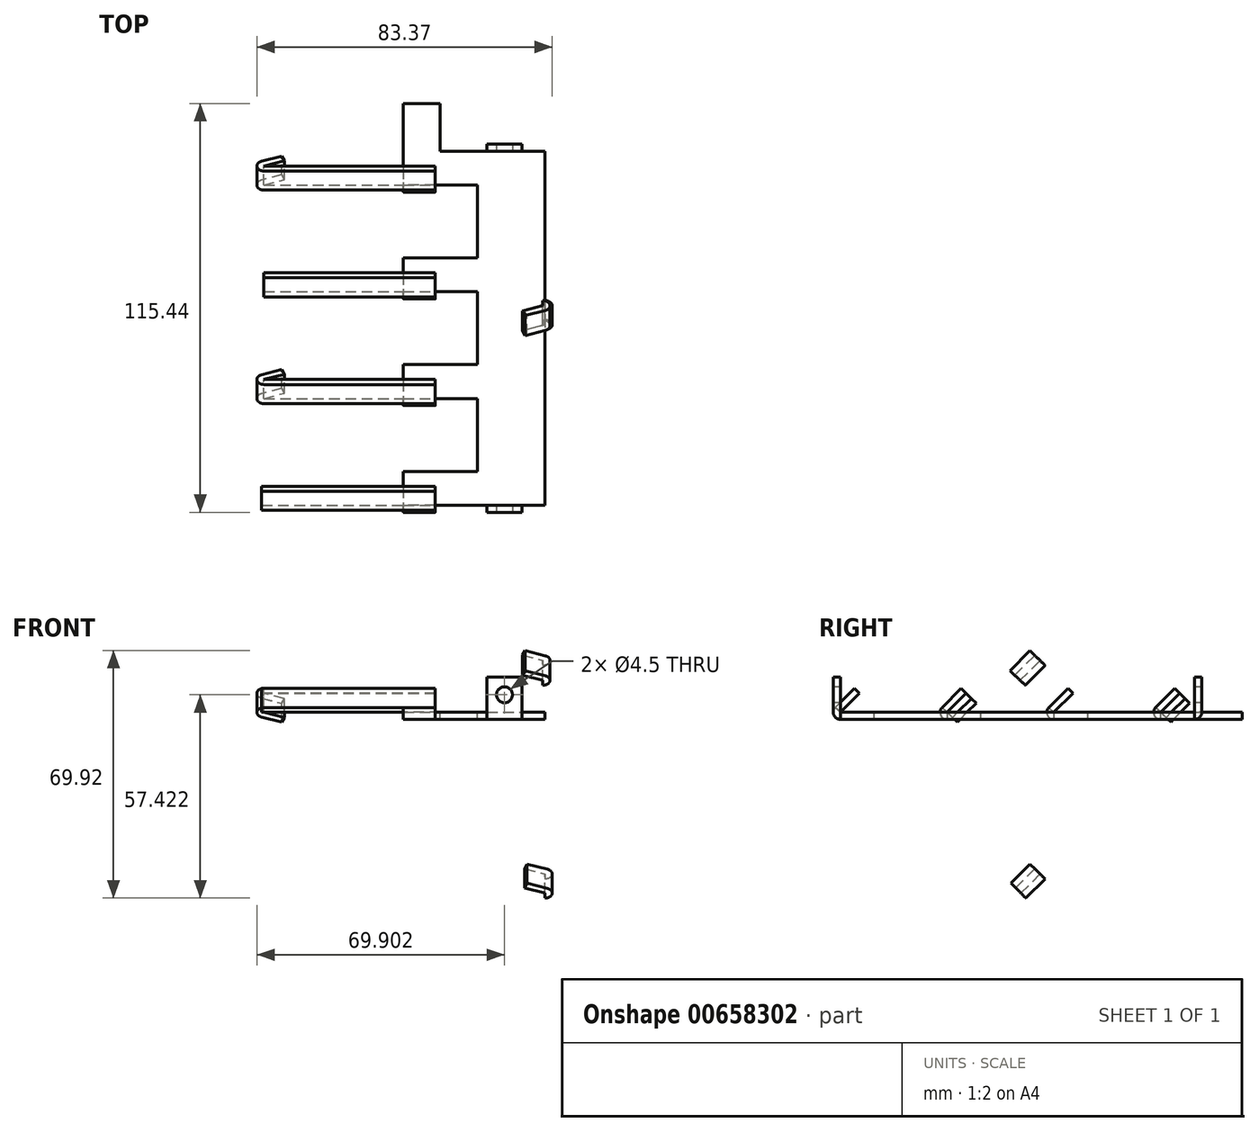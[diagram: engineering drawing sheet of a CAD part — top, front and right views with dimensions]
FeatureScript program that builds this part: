
annotation { "Feature Type Name" : "Feature", "Feature Type Description" : "" }
export const myFeature = defineFeature(function(context is Context, id is Id, definition is map)
    precondition{}
    {
        {
            var Q0;
            Q0=qCreatedBy(makeId("Top.planeOp"),FACE);
            var sketch = newSketch(context, id + "F0", { "sketchPlane" : qUnion([Q0])});
            skLineSegment(sketch, "E0", {"start": v(40, 50) * mm, "end": v(40, -50) * mm});
            skLineSegment(sketch, "E1", {"start": v(10.42, 50) * mm, "end": v(40, 50) * mm});
            skLineSegment(sketch, "E2", {"start": v(0, 50) * mm, "end": v(0, 40.43) * mm});
            skLineSegment(sketch, "E3", {"start": v(20.84, 40.43) * mm, "end": v(20.84, 19.86) * mm});
            skLineSegment(sketch, "E4", {"start": v(0, 19.86) * mm, "end": v(0, 10.29) * mm});
            skLineSegment(sketch, "E5", {"start": v(20.84, 10.29) * mm, "end": v(20.84, -10.29) * mm});
            skLineSegment(sketch, "E6", {"start": v(20.84, -10.29) * mm, "end": v(0, -10.29) * mm});
            skLineSegment(sketch, "E7", {"start": v(0, -10.29) * mm, "end": v(0, -19.86) * mm});
            skLineSegment(sketch, "E8", {"start": v(20.84, -19.86) * mm, "end": v(20.84, -40.43) * mm});
            skLineSegment(sketch, "E9", {"start": v(20.84, -40.43) * mm, "end": v(0, -40.43) * mm});
            skLineSegment(sketch, "E10", {"start": v(0, -40.43) * mm, "end": v(0, -50) * mm});
            skLineSegment(sketch, "E11", {"start": v(20.84, 19.86) * mm, "end": v(0, 19.86) * mm});
            skLineSegment(sketch, "E12", {"start": v(0, 40.43) * mm, "end": v(20.84, 40.43) * mm});
            skLineSegment(sketch, "E13", {"start": v(0, 10.29) * mm, "end": v(20.84, 10.29) * mm});
            skLineSegment(sketch, "E14", {"start": v(0, -19.86) * mm, "end": v(20.84, -19.86) * mm});
            skLineSegment(sketch, "E15", {"start": v(0, -50) * mm, "end": v(40, -50) * mm});
            skPoint(sketch, "E16.endSnap0", {"position": v(10.42, 40.43) * mm});
            skLineSegment(sketch, "E17", {"start": v(10.42, 50) * mm, "end": v(10.42, 63.44) * mm});
            skLineSegment(sketch, "E18", {"start": v(10.42, 63.44) * mm, "end": v(0, 63.44) * mm});
            skLineSegment(sketch, "E19", {"start": v(0, 63.44) * mm, "end": v(0, 50) * mm});
            skSolve(sketch);
        }
        {
            var Q0;
            Q0=makeQuery(id+"F0.imprint","IMPRINT",FACE,{"disambiguationData":[TD([[makeQuery(id+"F0.imprint","IMPRINT",EDGE,{"derivedFrom":sQuery(id+"F0.wireOp",EDGE,"E0")}),-1.0]])]});
            extrude(context, id + "F1", {"entities" : qUnion([Q0]), "endBound" : BoundingType.SYMMETRIC, "oppositeDirection" : true, "depth" : 2 * mm, "offsetDistance" : 25.4 * mm, "hasSecondDirection" : true, "secondDirectionOppositeDirection" : false, "secondDirectionDepth" : 0.76 * mm});
        }
        {
            var Q0;
            Q0=qCreatedBy(makeId("Right.planeOp"),FACE);
            var sketch = newSketch(context, id + "F2", { "sketchPlane" : qUnion([Q0])});
            skLineSegment(sketch, "E20", {"start": v(-50, 1) * mm, "end": v(-44.63, 6.37) * mm});
            skLineSegment(sketch, "E21", {"start": v(-44.63, 6.37) * mm, "end": v(-46.05, 7.78) * mm});
            skArc(sketch, "E22", {"start": v(-51.45, 2.37) * mm, "mid": v(-51.84, 0.2) * mm, "end": v(-50, -1) * mm});
            skLineSegment(sketch, "E23", {"start": v(-51.45, 2.37) * mm, "end": v(-46.05, 7.78) * mm});
            skLineSegment(sketch, "E24", {"start": v(-50, 1) * mm, "end": v(-50, -1) * mm});
            skLineSegment(sketch, "E25", {"start": v(-50, 1) * mm, "end": v(-51.45, 2.37) * mm});
            skSolve(sketch);
        }
        {
            var Q0;
            {var subQ1=sQuery(id+"F2.wireOp",EDGE,"E20");Q0=makeQuery(id+"F2.imprint","IMPRINT",FACE,{"disambiguationData":[TD([[makeQuery(id+"F2.imprint","IMPRINT",EDGE,{"derivedFrom":subQ1}),1.0]])]});}
            extrude(context, id + "F3", {"entities" : qUnion([Q0]), "operationType" : NewBodyOperationType.ADD, "oppositeDirection" : true, "depth" : 40 * mm, "offsetDistance" : 25.4 * mm});
        }
        {
            var Q0;
            Q0=makeQuery(id+"F3.opExtrude","SWEPT_FACE",FACE,{"disambiguationData":[OSD([sQuery(id+"F2.wireOp",EDGE,"E21")])]});
            var sketch = newSketch(context, id + "F4", { "sketchPlane" : qUnion([Q0])});
            skLineSegment(sketch, "E26", {"start": v(-40.68, -34.18) * mm, "end": v(-34.93, -32.09) * mm});
            skLineSegment(sketch, "E27", {"start": v(-34.93, -32.09) * mm, "end": v(-34.25, -33.97) * mm});
            skLineSegment(sketch, "E28", {"start": v(-34.25, -33.97) * mm, "end": v(-40, -36.06) * mm});
            skArc(sketch, "E29", {"start": v(-40.68, -34.18) * mm, "mid": v(-41.97, -36.4) * mm, "end": v(-40, -38.06) * mm});
            skLineSegment(sketch, "E30", {"start": v(-40, -36.06) * mm, "end": v(-40, -38.06) * mm});
            skSolve(sketch);
        }
        {
            var Q0;
            Q0=makeQuery(id+"F4.imprint","IMPRINT",FACE,{"disambiguationData":[TD([[makeQuery(id+"F4.imprint","IMPRINT",EDGE,{"derivedFrom":sQuery(id+"F4.wireOp",EDGE,"E26")}),-1.0]])]});
            extrude(context, id + "F5", {"entities" : qUnion([Q0]), "operationType" : NewBodyOperationType.ADD, "oppositeDirection" : true, "depth" : 7.65 * mm, "offsetDistance" : 25.4 * mm});
        }
        {
            var Q0;
            Q0=qCreatedBy(makeId("Right.planeOp"),FACE);
            var sketch = newSketch(context, id + "F6", { "sketchPlane" : qUnion([Q0])});
            skLineSegment(sketch, "E31", {"start": v(-19.86, 1) * mm, "end": v(-14.49, 6.36) * mm});
            skLineSegment(sketch, "E32", {"start": v(-14.49, 6.36) * mm, "end": v(-15.9, 7.78) * mm});
            skArc(sketch, "E33", {"start": v(-21.3, 2.37) * mm, "mid": v(-21.7, 0.2) * mm, "end": v(-19.86, -1) * mm});
            skLineSegment(sketch, "E34", {"start": v(-21.3, 2.37) * mm, "end": v(-15.9, 7.78) * mm});
            skLineSegment(sketch, "E35", {"start": v(-19.86, 1) * mm, "end": v(-19.86, -1) * mm});
            skLineSegment(sketch, "E36", {"start": v(-19.86, 1) * mm, "end": v(-21.3, 2.37) * mm});
            skSolve(sketch);
        }
        {
            var Q0;
            Q0=qCreatedBy(makeId("Right.planeOp"),FACE);
            var sketch = newSketch(context, id + "F7", { "sketchPlane" : qUnion([Q0])});
            skLineSegment(sketch, "E37", {"start": v(10.29, 1) * mm, "end": v(15.66, 6.36) * mm});
            skLineSegment(sketch, "E38", {"start": v(15.66, 6.36) * mm, "end": v(14.24, 7.78) * mm});
            skArc(sketch, "E39", {"start": v(8.84, 2.37) * mm, "mid": v(8.45, 0.2) * mm, "end": v(10.29, -1) * mm});
            skLineSegment(sketch, "E40", {"start": v(8.84, 2.37) * mm, "end": v(14.24, 7.78) * mm});
            skLineSegment(sketch, "E41", {"start": v(10.29, 1) * mm, "end": v(10.29, -1) * mm});
            skLineSegment(sketch, "E42", {"start": v(10.29, 1) * mm, "end": v(8.84, 2.37) * mm});
            skLineSegment(sketch, "E43", {"start": v(40.43, 1) * mm, "end": v(45.8, 6.37) * mm});
            skLineSegment(sketch, "E44", {"start": v(45.8, 6.37) * mm, "end": v(44.39, 7.78) * mm});
            skArc(sketch, "E45", {"start": v(38.98, 2.37) * mm, "mid": v(38.6, 0.2) * mm, "end": v(40.43, -1) * mm});
            skLineSegment(sketch, "E46", {"start": v(38.98, 2.37) * mm, "end": v(44.39, 7.78) * mm});
            skLineSegment(sketch, "E47", {"start": v(40.43, 1) * mm, "end": v(40.43, -1) * mm});
            skLineSegment(sketch, "E48", {"start": v(40.43, 1) * mm, "end": v(38.98, 2.37) * mm});
            skSolve(sketch);
        }
        {
            var Q0;
            Q0 = qSketchRegion(id + "F6", true);
            var Q1;
            {var subQ1=sQuery(id+"F2.wireOp",EDGE,"E20");Q1=makeQuery(id+"F2.imprint","IMPRINT",FACE,{"disambiguationData":[TD([[makeQuery(id+"F2.imprint","IMPRINT",EDGE,{"derivedFrom":subQ1}),1.0]])]});}
            var Q2;
            {var subQ0=sQuery(id+"F2.wireOp",EDGE,"E22");Q2=makeQuery(id+"F2.imprint","IMPRINT",FACE,{"disambiguationData":[TD([[makeQuery(id+"F2.imprint","IMPRINT",EDGE,{"derivedFrom":subQ0}),1.0]])]});}
            var Q3;
            {var subQ1=sQuery(id+"F7.wireOp",EDGE,"E37");Q3=makeQuery(id+"F7.imprint","IMPRINT",FACE,{"disambiguationData":[TD([[makeQuery(id+"F7.imprint","IMPRINT",EDGE,{"derivedFrom":subQ1}),1.0]])]});}
            var Q4;
            {var subQ0=sQuery(id+"F7.wireOp",EDGE,"E39");Q4=makeQuery(id+"F7.imprint","IMPRINT",FACE,{"disambiguationData":[TD([[makeQuery(id+"F7.imprint","IMPRINT",EDGE,{"derivedFrom":subQ0}),1.0]])]});}
            var Q5;
            {var subQ1=sQuery(id+"F7.wireOp",EDGE,"E43");Q5=makeQuery(id+"F7.imprint","IMPRINT",FACE,{"disambiguationData":[TD([[makeQuery(id+"F7.imprint","IMPRINT",EDGE,{"derivedFrom":subQ1}),1.0]])]});}
            var Q6;
            {var subQ0=sQuery(id+"F7.wireOp",EDGE,"E45");Q6=makeQuery(id+"F7.imprint","IMPRINT",FACE,{"disambiguationData":[TD([[makeQuery(id+"F7.imprint","IMPRINT",EDGE,{"derivedFrom":subQ0}),1.0]])]});}
            var Q7;
            Q7=makeQuery(id+"FUqeAPM6QKtiatm_4.opExtrude","CAP_FACE",FACE,{"disambiguationData":[OSD([sQuery(id+"F2.wireOp",EDGE,"E20"),sQuery(id+"F2.wireOp",EDGE,"E21"),sQuery(id+"F2.wireOp",EDGE,"E22"),sQuery(id+"F2.wireOp",EDGE,"E23"),sQuery(id+"F2.wireOp",EDGE,"E24")])],"isStart":false});
            extrude(context, id + "F8", {"entities" : qUnion([Q0, Q1, Q2, Q3, Q4, Q5, Q6]), "operationType" : NewBodyOperationType.ADD, "depth" : 9 * mm, "endBoundEntityFace" : qUnion([Q7]), "offsetDistance" : 25.4 * mm});
        }
        {
            var Q0;
            {var subQ1=sQuery(id+"F6.wireOp",EDGE,"E31");Q0=makeQuery(id+"F6.imprint","IMPRINT",FACE,{"disambiguationData":[TD([[makeQuery(id+"F6.imprint","IMPRINT",EDGE,{"derivedFrom":subQ1}),1.0]])]});}
            var Q1;
            {var subQ1=sQuery(id+"F7.wireOp",EDGE,"E37");Q1=makeQuery(id+"F7.imprint","IMPRINT",FACE,{"disambiguationData":[TD([[makeQuery(id+"F7.imprint","IMPRINT",EDGE,{"derivedFrom":subQ1}),1.0]])]});}
            var Q2;
            {var subQ1=sQuery(id+"F7.wireOp",EDGE,"E43");Q2=makeQuery(id+"F7.imprint","IMPRINT",FACE,{"disambiguationData":[TD([[makeQuery(id+"F7.imprint","IMPRINT",EDGE,{"derivedFrom":subQ1}),1.0]])]});}
            extrude(context, id + "F9", {"entities" : qUnion([Q0, Q1, Q2]), "operationType" : NewBodyOperationType.ADD, "oppositeDirection" : true, "depth" : 39.37 * mm, "offsetDistance" : 25.4 * mm});
        }
        {
            var Q0;
            {var subQ0=sQuery(id+"F6.wireOp",EDGE,"E32");Q0=makeQuery(id+"F9.boolean.opBoolean","MERGE",FACE,{"derivedFrom":[makeQuery(id+"F8.opExtrude","SWEPT_FACE",FACE,{"disambiguationData":[OSD([subQ0])]}),makeQuery(id+"F9.opExtrude","SWEPT_FACE",FACE,{"disambiguationData":[OSD([subQ0])]})]});}
            var sketch = newSketch(context, id + "F10", { "sketchPlane" : qUnion([Q0])});
            skLineSegment(sketch, "E49", {"start": v(40.05, 12.86) * mm, "end": v(34.3, 10.77) * mm});
            skLineSegment(sketch, "E50", {"start": v(34.3, 10.77) * mm, "end": v(33.62, 12.65) * mm});
            skLineSegment(sketch, "E51", {"start": v(33.62, 12.65) * mm, "end": v(39.37, 14.74) * mm});
            skArc(sketch, "E52", {"start": v(40.05, 12.86) * mm, "mid": v(41.34, 15.1) * mm, "end": v(39.37, 16.74) * mm});
            skLineSegment(sketch, "E53", {"start": v(39.37, 14.74) * mm, "end": v(39.37, 16.74) * mm});
            skSolve(sketch);
        }
        {
            var Q0;
            Q0 = qSketchRegion(id + "F10", true);
            var Q1;
            Q1=makeQuery(id+"F9.opExtrude","SWEPT_FACE",FACE,{"disambiguationData":[OSD([sQuery(id+"F6.wireOp",EDGE,"E36")])]});
            extrude(context, id + "F11", {"entities" : qUnion([Q0]), "operationType" : NewBodyOperationType.ADD, "endBound" : BoundingType.UP_TO_SURFACE, "oppositeDirection" : true, "depth" : 25.4 * mm, "endBoundEntityFace" : qUnion([Q1]), "offsetDistance" : 25.4 * mm});
        }
        {
            var Q0;
            {var subQ0=sQuery(id+"F7.wireOp",EDGE,"E38");Q0=makeQuery(id+"F9.boolean.opBoolean","MERGE",FACE,{"derivedFrom":[makeQuery(id+"F8.opExtrude","SWEPT_FACE",FACE,{"disambiguationData":[OSD([subQ0])]}),makeQuery(id+"F9.opExtrude","SWEPT_FACE",FACE,{"disambiguationData":[OSD([subQ0])]})]});}
            var sketch = newSketch(context, id + "F12", { "sketchPlane" : qUnion([Q0])});
            skLineSegment(sketch, "E54", {"start": v(-40.05, 8.45) * mm, "end": v(-34.3, 10.55) * mm});
            skLineSegment(sketch, "E55", {"start": v(-34.3, 10.55) * mm, "end": v(-33.62, 8.67) * mm});
            skLineSegment(sketch, "E56", {"start": v(-33.62, 8.67) * mm, "end": v(-39.37, 6.57) * mm});
            skArc(sketch, "E57", {"start": v(-40.05, 8.45) * mm, "mid": v(-41.34, 6.22) * mm, "end": v(-39.37, 4.57) * mm});
            skLineSegment(sketch, "E58", {"start": v(-39.37, 6.57) * mm, "end": v(-39.37, 4.57) * mm});
            skSolve(sketch);
        }
        {
            var Q0;
            Q0 = qSketchRegion(id + "F12", true);
            var Q1;
            Q1=makeQuery(id+"F9.opExtrude","SWEPT_FACE",FACE,{"disambiguationData":[OSD([sQuery(id+"F7.wireOp",EDGE,"E42")])]});
            extrude(context, id + "F13", {"entities" : qUnion([Q0]), "operationType" : NewBodyOperationType.ADD, "endBound" : BoundingType.UP_TO_SURFACE, "oppositeDirection" : true, "depth" : 25.4 * mm, "endBoundEntityFace" : qUnion([Q1]), "offsetDistance" : 25.4 * mm});
        }
        {
            var Q0;
            {var subQ0=sQuery(id+"F7.wireOp",EDGE,"E44");Q0=makeQuery(id+"F9.boolean.opBoolean","MERGE",FACE,{"derivedFrom":[makeQuery(id+"F8.opExtrude","SWEPT_FACE",FACE,{"disambiguationData":[OSD([subQ0])]}),makeQuery(id+"F9.opExtrude","SWEPT_FACE",FACE,{"disambiguationData":[OSD([subQ0])]})]});}
            var sketch = newSketch(context, id + "F14", { "sketchPlane" : qUnion([Q0])});
            skLineSegment(sketch, "E59", {"start": v(40.05, -29.76) * mm, "end": v(34.3, -31.86) * mm});
            skLineSegment(sketch, "E60", {"start": v(34.3, -31.86) * mm, "end": v(33.62, -29.98) * mm});
            skLineSegment(sketch, "E61", {"start": v(33.62, -29.98) * mm, "end": v(39.37, -27.89) * mm});
            skArc(sketch, "E62", {"start": v(40.05, -29.76) * mm, "mid": v(41.34, -27.54) * mm, "end": v(39.37, -25.89) * mm});
            skLineSegment(sketch, "E63", {"start": v(39.37, -27.89) * mm, "end": v(39.37, -25.89) * mm});
            skSolve(sketch);
        }
        {
            var Q0;
            Q0 = qSketchRegion(id + "F14", true);
            var Q1;
            Q1=makeQuery(id+"F9.opExtrude","SWEPT_FACE",FACE,{"disambiguationData":[OSD([sQuery(id+"F7.wireOp",EDGE,"E48")])]});
            extrude(context, id + "F15", {"entities" : qUnion([Q0]), "operationType" : NewBodyOperationType.ADD, "endBound" : BoundingType.UP_TO_SURFACE, "oppositeDirection" : true, "depth" : 25.4 * mm, "endBoundEntityFace" : qUnion([Q1]), "offsetDistance" : 25.4 * mm});
        }
        {
            var Q0;
            Q0=makeQuery(id+"F1.opExtrude","SWEPT_FACE",FACE,{"disambiguationData":[OSD([sQuery(id+"F0.wireOp",EDGE,"E1")])]});
            var sketch = newSketch(context, id + "F16", { "sketchPlane" : qUnion([Q0])});
            skLineSegment(sketch, "E64.bottom", {"start": v(-23.57, -1) * mm, "end": v(-33.5, -1) * mm});
            skLineSegment(sketch, "E64.top", {"start": v(-23.57, 10.94) * mm, "end": v(-33.5, 10.94) * mm});
            skLineSegment(sketch, "E64.left", {"start": v(-23.57, -1) * mm, "end": v(-23.57, 10.94) * mm});
            skLineSegment(sketch, "E64.right", {"start": v(-33.5, -1) * mm, "end": v(-33.5, 10.94) * mm});
            skSolve(sketch);
        }
        {
            var Q0;
            Q0 = qSketchRegion(id + "F16", true);
            extrude(context, id + "F17", {"entities" : qUnion([Q0]), "operationType" : NewBodyOperationType.ADD, "depth" : 2 * mm, "offsetDistance" : 25.4 * mm});
        }
        {
            var Q0;
            {var subQ4=sQuery(id+"F0.wireOp",EDGE,"E15");var subQ18=sQuery(id+"F0.wireOp",EDGE,"E0");var subQ20=sQuery(id+"F2.wireOp",EDGE,"E24");Q0=makeQuery(id+"F8.boolean.opBoolean","SPLIT",FACE,{"disambiguationData":[TD([makeQuery(id+"F1.opExtrude","SWEPT_FACE",FACE,{"disambiguationData":[OSD([subQ18])]})])],"derivedFrom":makeQuery(id+"F3.boolean.opBoolean","MERGE",FACE,{"derivedFrom":[makeQuery(id+"F1.opExtrude","SWEPT_FACE",FACE,{"disambiguationData":[OSD([subQ4])]}),makeQuery(id+"F3.opExtrude","SWEPT_FACE",FACE,{"disambiguationData":[OSD([subQ20])]})]})});}
            var sketch = newSketch(context, id + "F18", { "sketchPlane" : qUnion([Q0])});
            skLineSegment(sketch, "E65.bottom", {"start": v(33.5, -1) * mm, "end": v(23.57, -1) * mm});
            skLineSegment(sketch, "E65.top", {"start": v(33.5, 10.94) * mm, "end": v(23.57, 10.94) * mm});
            skLineSegment(sketch, "E65.left", {"start": v(33.5, -1) * mm, "end": v(33.5, 10.94) * mm});
            skLineSegment(sketch, "E65.right", {"start": v(23.57, -1) * mm, "end": v(23.57, 10.94) * mm});
            skSolve(sketch);
        }
        {
            var Q0;
            Q0 = qSketchRegion(id + "F18", true);
            extrude(context, id + "F19", {"entities" : qUnion([Q0]), "operationType" : NewBodyOperationType.ADD, "depth" : 2 * mm, "offsetDistance" : 25.4 * mm});
        }
        {
            var Q0;
            Q0=makeQuery(id+"F19.opExtrude","CAP_EDGE",EDGE,{"disambiguationData":[OSD([sQuery(id+"F18.wireOp",EDGE,"E65.bottom")])],"isStart":false});
            var Q1;
            Q1=makeQuery(id+"F17.opExtrude","CAP_EDGE",EDGE,{"disambiguationData":[OSD([sQuery(id+"F16.wireOp",EDGE,"E64.bottom")])],"isStart":false});
            fillet(context, id + "F20", {"entities" : qUnion([Q0, Q1]), "radius" : 2 * mm, "tangentPropagation" : true, "allowEdgeOverflow" : false});
        }
        {
            var Q0;
            Q0=makeQuery(id+"F19.opExtrude","CAP_FACE",FACE,{"disambiguationData":[OSD([sQuery(id+"F18.wireOp",EDGE,"E65.bottom"),sQuery(id+"F18.wireOp",EDGE,"E65.top"),sQuery(id+"F18.wireOp",EDGE,"E65.left"),sQuery(id+"F18.wireOp",EDGE,"E65.right")])],"isStart":false});
            var sketch = newSketch(context, id + "F21", { "sketchPlane" : qUnion([Q0])});
            skCircle(sketch, "E66", {"center": v(28.53, 5.97) * mm, "radius": 1.47 * mm});
            skSolve(sketch);
        }
        {
            var Q0;
            Q0=sQuery(id+"F21.wireOp",VERTEX,"E66.center");
            var Q1;
            Q1=makeQuery(id+"F1.opExtrude","SWEPT_BODY",BODY,{"disambiguationData":[OSD([sQuery(id+"F0.wireOp",EDGE,"E0"),sQuery(id+"F0.wireOp",EDGE,"E1"),sQuery(id+"F0.wireOp",EDGE,"E2"),sQuery(id+"F0.wireOp",EDGE,"E3"),sQuery(id+"F0.wireOp",EDGE,"E4"),sQuery(id+"F0.wireOp",EDGE,"E5"),sQuery(id+"F0.wireOp",EDGE,"E6"),sQuery(id+"F0.wireOp",EDGE,"E7"),sQuery(id+"F0.wireOp",EDGE,"E8"),sQuery(id+"F0.wireOp",EDGE,"E9"),sQuery(id+"F0.wireOp",EDGE,"E10"),sQuery(id+"F0.wireOp",EDGE,"E11"),sQuery(id+"F0.wireOp",EDGE,"E12"),sQuery(id+"F0.wireOp",EDGE,"E13"),sQuery(id+"F0.wireOp",EDGE,"E14"),sQuery(id+"F0.wireOp",EDGE,"E15"),sQuery(id+"F0.wireOp",EDGE,"E17"),sQuery(id+"F0.wireOp",EDGE,"E18"),sQuery(id+"F0.wireOp",EDGE,"E19")])]});
            hole(context, id + "F22", {"style" : HoleStyle.SIMPLE, "endStyle" : HoleEndStyle.THROUGH, "holeDiameter" : 4.5 * mm, "majorDiameter" : 6.35 * mm, "isTappedThrough" : true, "tappedDepth" : 12.7 * mm, "tapClearance" : 3, "locations" : qUnion([Q0]), "scope" : qUnion([Q1])});
        }
    });
